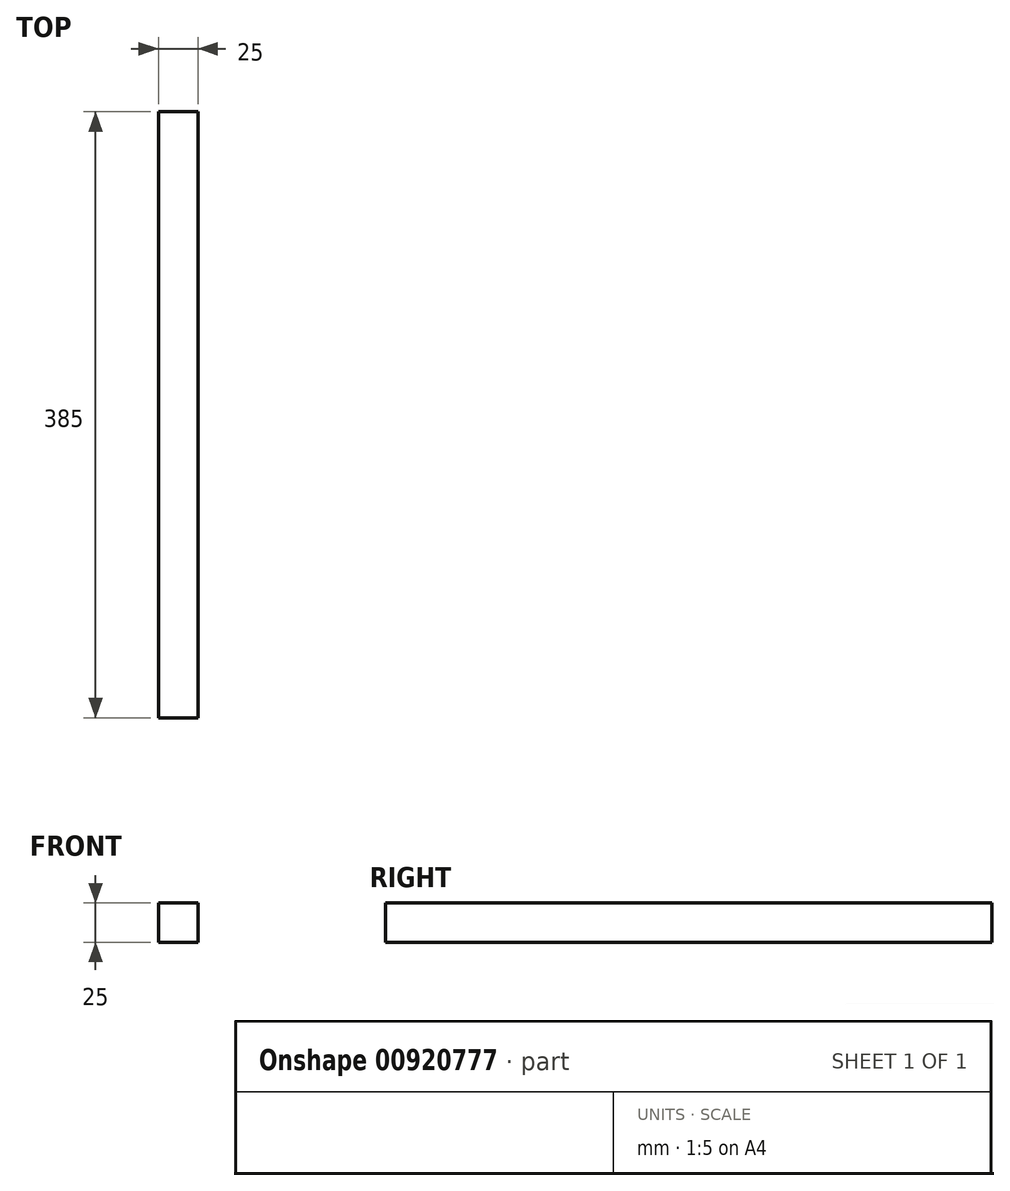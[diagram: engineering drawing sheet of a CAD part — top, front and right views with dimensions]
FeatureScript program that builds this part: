
annotation { "Feature Type Name" : "Feature", "Feature Type Description" : "" }
export const myFeature = defineFeature(function(context is Context, id is Id, definition is map)
    precondition{}
    {
        {
            var Q0;
            Q0=qCreatedBy(makeId("Front.planeOp"),FACE);
            var sketch = newSketch(context, id + "F0", { "sketchPlane" : qUnion([Q0])});
            skLineSegment(sketch, "E0.bottom", {"start": v(12.5, 12.5) * mm, "end": v(-12.5, 12.5) * mm});
            skLineSegment(sketch, "E0.top", {"start": v(12.5, -12.5) * mm, "end": v(-12.5, -12.5) * mm});
            skLineSegment(sketch, "E0.left", {"start": v(12.5, 12.5) * mm, "end": v(12.5, -12.5) * mm});
            skLineSegment(sketch, "E0.right", {"start": v(-12.5, 12.5) * mm, "end": v(-12.5, -12.5) * mm});
            skPoint(sketch, "E0.middle", {"position": v(0, 0) * mm});
            skSolve(sketch);
        }
        {
            var Q0;
            Q0 = qSketchRegion(id + "F0", true);
            extrude(context, id + "F1", {"entities" : qUnion([Q0]), "depth" : 385 * mm, "offsetDistance" : 25 * mm});
        }
    });
